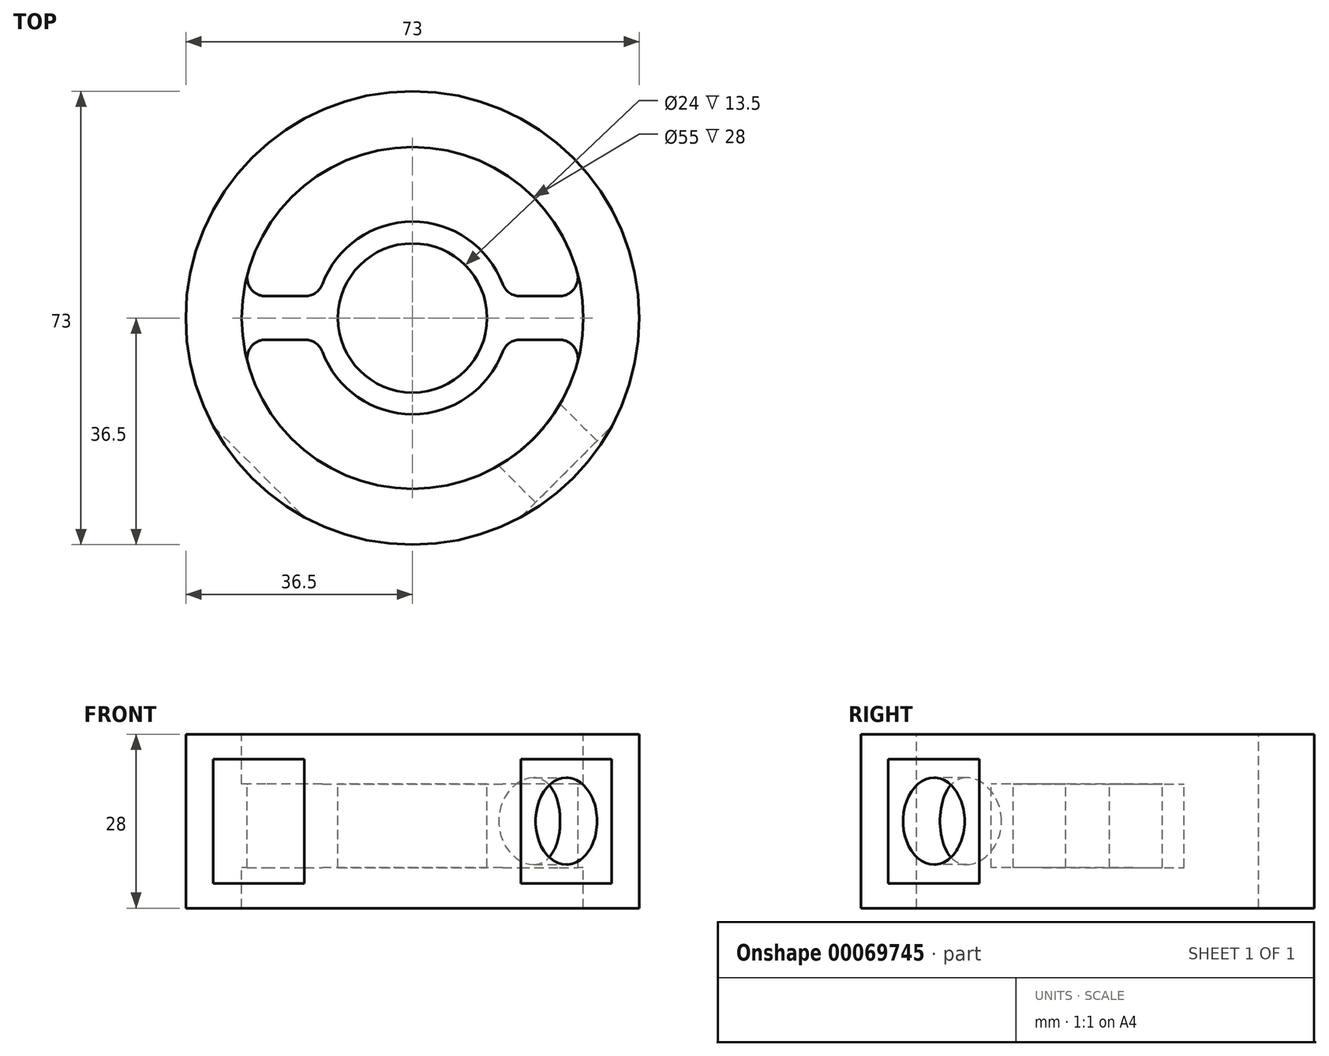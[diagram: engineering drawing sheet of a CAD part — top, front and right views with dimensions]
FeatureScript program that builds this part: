
annotation { "Feature Type Name" : "Feature", "Feature Type Description" : "" }
export const myFeature = defineFeature(function(context is Context, id is Id, definition is map)
    precondition{}
    {
        {
            var Q0;
            Q0=qCreatedBy(makeId("Top.planeOp"),FACE);
            var sketch = newSketch(context, id + "F0", { "sketchPlane" : qUnion([Q0])});
            skCircle(sketch, "E0", {"center": v(0, 0) * mm, "radius": 36.5 * mm});
            skSolve(sketch);
        }
        {
            var Q0;
            Q0=makeQuery(id+"F0.imprint","IMPRINT",FACE,{"disambiguationData":[TD([[makeQuery(id+"F0.imprint","IMPRINT",EDGE,{"derivedFrom":sQuery(id+"F0.wireOp",EDGE,"E0")}),1.0]])]});
            extrude(context, id + "F1", {"entities" : qUnion([Q0]), "endBound" : BoundingType.SYMMETRIC, "depth" : 28 * mm});
        }
        {
            var Q0;
            Q0=makeQuery(id+"F1.opExtrude","CAP_FACE",FACE,{"disambiguationData":[OSD([sQuery(id+"F0.wireOp",EDGE,"E0")])],"isStart":false});
            var sketch = newSketch(context, id + "F2", { "sketchPlane" : qUnion([Q0])});
            skArc(sketch, "E1", {"start": v(-27.28, -3.5) * mm, "mid": v(0, -27.5) * mm, "end": v(27.28, -3.5) * mm});
            skArc(sketch, "E2", {"start": v(-15.1, -3.5) * mm, "mid": v(0, -15.5) * mm, "end": v(15.1, -3.5) * mm});
            skCircle(sketch, "E3", {"center": v(0, 0) * mm, "radius": 12 * mm});
            skLineSegment(sketch, "E4", {"start": v(-27.28, -3.5) * mm, "end": v(-15.1, -3.5) * mm});
            skLineSegment(sketch, "E5", {"start": v(-27.28, 3.5) * mm, "end": v(-15.1, 3.5) * mm});
            skLineSegment(sketch, "E6.trimOffspring", {"start": v(15.1, 3.5) * mm, "end": v(27.28, 3.5) * mm});
            skLineSegment(sketch, "E7.trimOffspring", {"start": v(15.1, -3.5) * mm, "end": v(27.28, -3.5) * mm});
            skArc(sketch, "E8.trimOffspring", {"start": v(15.1, 3.5) * mm, "mid": v(0, 15.5) * mm, "end": v(-15.1, 3.5) * mm});
            skArc(sketch, "E9.trimOffspring", {"start": v(27.28, 3.5) * mm, "mid": v(0, 27.5) * mm, "end": v(-27.28, 3.5) * mm});
            skSolve(sketch);
        }
        {
            var Q0;
            Q0 = qSketchRegion(id + "F2", true);
            extrude(context, id + "F3", {"entities" : qUnion([Q0]), "operationType" : NewBodyOperationType.REMOVE, "endBound" : BoundingType.THROUGH_ALL, "oppositeDirection" : true, "depth" : 25 * mm});
        }
        {
            var Q0;
            Q0=makeQuery(id+"F3.boolean.opBoolean","COPY",EDGE,{"derivedFrom":makeQuery(id+"F3.opExtrude","SWEPT_EDGE",EDGE,{"disambiguationData":[OSD([sQuery(id+"F2.wireOp",EDGE,"E5"),sQuery(id+"F2.wireOp",EDGE,"E9.trimOffspring")])]})});
            var Q1;
            Q1=makeQuery(id+"F3.boolean.opBoolean","COPY",EDGE,{"derivedFrom":makeQuery(id+"F3.opExtrude","SWEPT_EDGE",EDGE,{"disambiguationData":[OSD([sQuery(id+"F2.wireOp",EDGE,"E5"),sQuery(id+"F2.wireOp",EDGE,"E8.trimOffspring")])]})});
            var Q2;
            Q2=makeQuery(id+"F3.boolean.opBoolean","COPY",EDGE,{"derivedFrom":makeQuery(id+"F3.opExtrude","SWEPT_EDGE",EDGE,{"disambiguationData":[OSD([sQuery(id+"F2.wireOp",EDGE,"E6.trimOffspring"),sQuery(id+"F2.wireOp",EDGE,"E8.trimOffspring")])]})});
            var Q3;
            Q3=makeQuery(id+"F3.boolean.opBoolean","COPY",EDGE,{"derivedFrom":makeQuery(id+"F3.opExtrude","SWEPT_EDGE",EDGE,{"disambiguationData":[OSD([sQuery(id+"F2.wireOp",EDGE,"E6.trimOffspring"),sQuery(id+"F2.wireOp",EDGE,"E9.trimOffspring")])]})});
            var Q4;
            Q4=makeQuery(id+"F3.boolean.opBoolean","COPY",EDGE,{"derivedFrom":makeQuery(id+"F3.opExtrude","SWEPT_EDGE",EDGE,{"disambiguationData":[OSD([sQuery(id+"F2.wireOp",EDGE,"E1"),sQuery(id+"F2.wireOp",EDGE,"E7.trimOffspring")])]})});
            var Q5;
            Q5=makeQuery(id+"F3.boolean.opBoolean","COPY",EDGE,{"derivedFrom":makeQuery(id+"F3.opExtrude","SWEPT_EDGE",EDGE,{"disambiguationData":[OSD([sQuery(id+"F2.wireOp",EDGE,"E2"),sQuery(id+"F2.wireOp",EDGE,"E7.trimOffspring")])]})});
            var Q6;
            Q6=makeQuery(id+"F3.boolean.opBoolean","COPY",EDGE,{"derivedFrom":makeQuery(id+"F3.opExtrude","SWEPT_EDGE",EDGE,{"disambiguationData":[OSD([sQuery(id+"F2.wireOp",EDGE,"E2"),sQuery(id+"F2.wireOp",EDGE,"E4")])]})});
            var Q7;
            Q7=makeQuery(id+"F3.boolean.opBoolean","COPY",EDGE,{"derivedFrom":makeQuery(id+"F3.opExtrude","SWEPT_EDGE",EDGE,{"disambiguationData":[OSD([sQuery(id+"F2.wireOp",EDGE,"E1"),sQuery(id+"F2.wireOp",EDGE,"E4")])]})});
            fillet(context, id + "F4", {"entities" : qUnion([Q0, Q1, Q2, Q3, Q4, Q5, Q6, Q7]), "radius" : 3 * mm, "tangentPropagation" : true, "allowEdgeOverflow" : false});
        }
        {
            var Q0;
            Q0=makeQuery(id+"F1.opExtrude","CAP_FACE",FACE,{"disambiguationData":[OSD([sQuery(id+"F0.wireOp",EDGE,"E0")])],"isStart":false});
            var sketch = newSketch(context, id + "F5", { "sketchPlane" : qUnion([Q0])});
            skCircle(sketch, "E10", {"center": v(0, 0) * mm, "radius": 27.5 * mm});
            skSolve(sketch);
        }
        {
            var Q0;
            Q0 = qSketchRegion(id + "F5", true);
            extrude(context, id + "F6", {"entities" : qUnion([Q0]), "operationType" : NewBodyOperationType.REMOVE, "oppositeDirection" : true, "depth" : 8 * mm});
        }
        {
            var Q0;
            Q0=makeQuery(id+"F1.opExtrude","CAP_FACE",FACE,{"disambiguationData":[OSD([sQuery(id+"F0.wireOp",EDGE,"E0")])],"isStart":true});
            var sketch = newSketch(context, id + "F7", { "sketchPlane" : qUnion([Q0])});
            skCircle(sketch, "E11", {"center": v(0, 0) * mm, "radius": 27.5 * mm});
            skSolve(sketch);
        }
        {
            var Q0;
            Q0 = qSketchRegion(id + "F7", true);
            extrude(context, id + "F8", {"entities" : qUnion([Q0]), "operationType" : NewBodyOperationType.REMOVE, "oppositeDirection" : true, "depth" : 6.5 * mm});
        }
        {
            var Q0;
            Q0=qCreatedBy(makeId("Top.planeOp"),FACE);
            var sketch = newSketch(context, id + "F9", { "sketchPlane" : qUnion([Q0])});
            skLineSegment(sketch, "E12", {"start": v(-40, -9.5) * mm, "end": v(0, -49.5) * mm});
            skLineSegment(sketch, "E13", {"start": v(0, -49.5) * mm, "end": v(40, -9.5) * mm});
            skLineSegment(sketch, "E14", {"start": v(-40, -9.5) * mm, "end": v(-40, -49.5) * mm});
            skLineSegment(sketch, "E15", {"start": v(-40, -49.5) * mm, "end": v(0, -49.5) * mm});
            skLineSegment(sketch, "E16", {"start": v(40, -9.5) * mm, "end": v(40, -49.5) * mm});
            skLineSegment(sketch, "E17", {"start": v(40, -49.5) * mm, "end": v(0, -49.5) * mm});
            skSolve(sketch);
        }
        {
            var Q0;
            Q0=makeQuery(id+"F9.imprint","IMPRINT",FACE,{"disambiguationData":[TD([[makeQuery(id+"F9.imprint","IMPRINT",EDGE,{"derivedFrom":sQuery(id+"F9.wireOp",EDGE,"E12")}),-1.0]])]});
            var Q1;
            Q1=makeQuery(id+"F9.imprint","IMPRINT",FACE,{"disambiguationData":[TD([[makeQuery(id+"F9.imprint","IMPRINT",EDGE,{"derivedFrom":sQuery(id+"F9.wireOp",EDGE,"E13")}),-1.0]])]});
            extrude(context, id + "F10", {"entities" : qUnion([Q0, Q1]), "operationType" : NewBodyOperationType.REMOVE, "endBound" : BoundingType.SYMMETRIC, "oppositeDirection" : true, "depth" : 20 * mm});
        }
        {
            var Q0;
            Q0=makeQuery(id+"F10.boolean.opBoolean","COPY",FACE,{"derivedFrom":makeQuery(id+"F10.opExtrude","SWEPT_FACE",FACE,{"disambiguationData":[OSD([sQuery(id+"F9.wireOp",EDGE,"E13")])]})});
            var sketch = newSketch(context, id + "F11", { "sketchPlane" : qUnion([Q0])});
            skCircle(sketch, "E18", {"center": v(0, 0) * mm, "radius": 7 * mm});
            skSolve(sketch);
        }
        {
            var Q0;
            Q0 = qSketchRegion(id + "F11", true);
            extrude(context, id + "F12", {"entities" : qUnion([Q0]), "operationType" : NewBodyOperationType.REMOVE, "oppositeDirection" : true, "depth" : 10 * mm});
        }
    });
